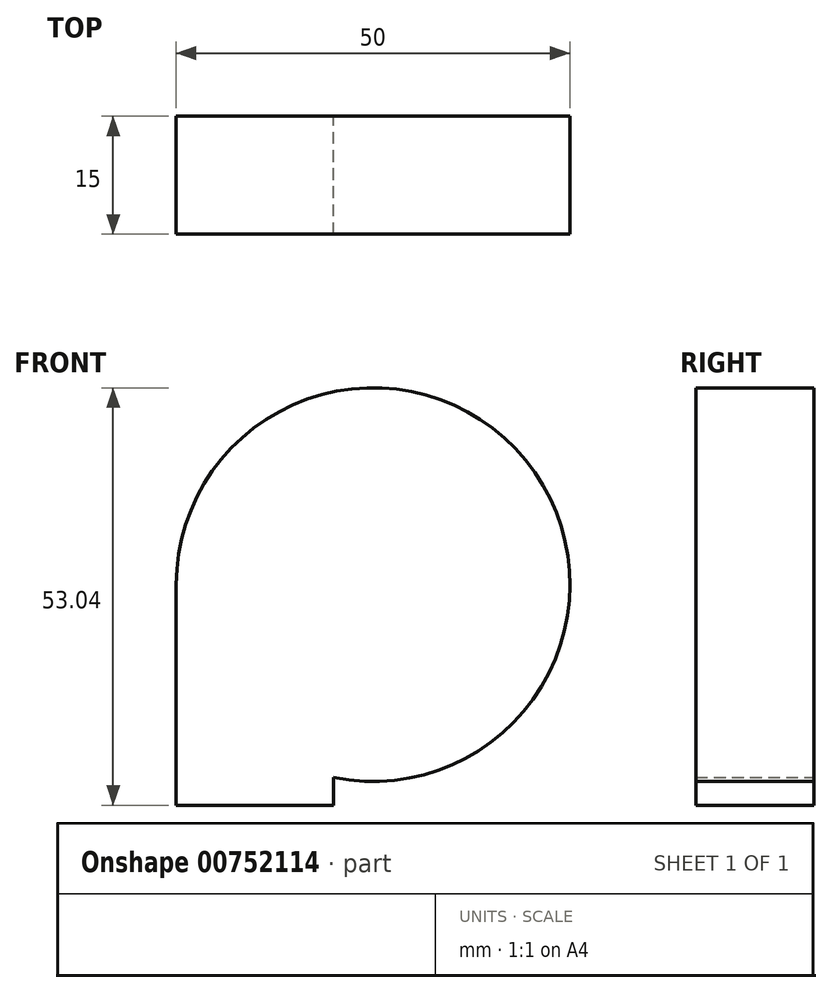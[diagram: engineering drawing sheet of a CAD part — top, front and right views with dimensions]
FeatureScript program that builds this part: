
annotation { "Feature Type Name" : "Feature", "Feature Type Description" : "" }
export const myFeature = defineFeature(function(context is Context, id is Id, definition is map)
    precondition{}
    {
        {
            var Q0;
            Q0=qCreatedBy(makeId("Front.planeOp"),FACE);
            var sketch = newSketch(context, id + "F0", { "sketchPlane" : qUnion([Q0])});
            skArc(sketch, "E0", {"start": v(-5, -24.5) * mm, "mid": v(19.37, 15.81) * mm, "end": v(-25, 0) * mm});
            skLineSegment(sketch, "E1.top", {"start": v(-25, -28.04) * mm, "end": v(-5, -28.04) * mm});
            skLineSegment(sketch, "E1.left", {"start": v(-25, 0) * mm, "end": v(-25, -28.04) * mm});
            skLineSegment(sketch, "E1.right", {"start": v(-5, -24.5) * mm, "end": v(-5, -28.04) * mm});
            skSolve(sketch);
        }
        {
            var Q0;
            Q0 = qSketchRegion(id + "F0", true);
            extrude(context, id + "F1", {"entities" : qUnion([Q0]), "depth" : 15 * mm, "offsetDistance" : 25.4 * mm});
        }
    });
